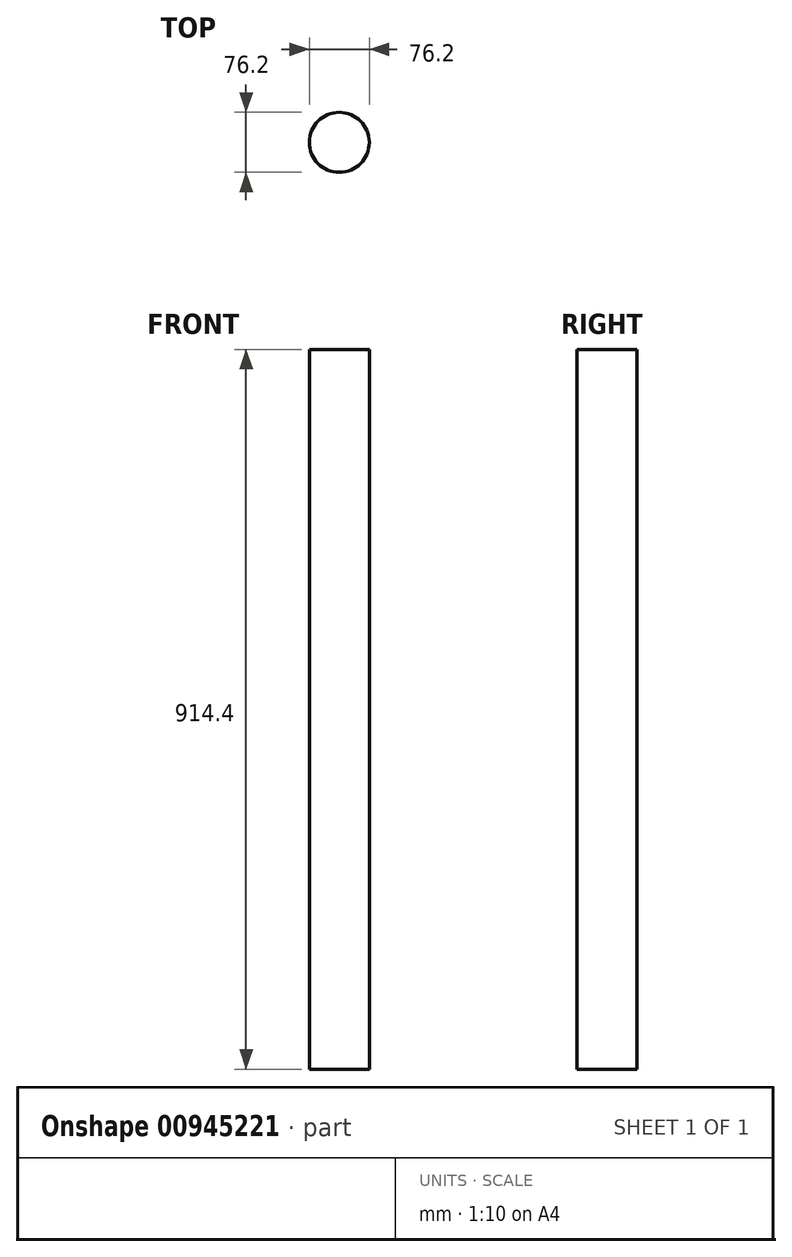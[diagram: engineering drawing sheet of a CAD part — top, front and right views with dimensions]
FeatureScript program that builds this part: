
annotation { "Feature Type Name" : "Feature", "Feature Type Description" : "" }
export const myFeature = defineFeature(function(context is Context, id is Id, definition is map)
    precondition{}
    {
        {
            var Q0;
            Q0=qCreatedBy(makeId("Top.planeOp"),FACE);
            var sketch = newSketch(context, id + "F0", { "sketchPlane" : qUnion([Q0])});
            skCircle(sketch, "E0", {"center": v(0, 0) * mm, "radius": 38.1 * mm});
            skSolve(sketch);
        }
        {
            var Q0;
            Q0=makeQuery(id+"F0.imprint","IMPRINT",FACE,{"disambiguationData":[TD([[makeQuery(id+"F0.imprint","IMPRINT",EDGE,{"derivedFrom":sQuery(id+"F0.wireOp",EDGE,"E0")}),1.0]])]});
            extrude(context, id + "F1", {"entities" : qUnion([Q0]), "depth" : 914.4 * mm, "offsetDistance" : 25.4 * mm});
        }
    });
